# Revit family: Projector_Mount_Accessory-Chief-Extension-Fixed-CMS006
name_source: partatom
category: Specialty Equipment
revit_build: Autodesk Revit MEP 2012 (Build: 20110309_2315(x64)
units: mm (PartAtom-declared; Revit-internal decimal feet)

## types (3) — shared parameters
04 CSI = 11 52 00
95 CSI = 11130
Assembly Code = E1020500
CAD Drawings URL = http://downloads.chiefmfg.com
Certification = TÜV Certified, UL Listed
Cost Info = http://www.chiefmfg.com
Description = Projector Mount Accessory - Extension Column, Fixed
Height = 0' - 1 29/32"
Manual and Installation URL = http://downloads.chiefmfg.com
Manufacturer = Chief
Manufacturer Fax = 877.894.6918
Product Line = Extension-Fixed
Product Page URL = http://www.chiefmfg.com
Subcategory = Projector Mount Accessories
URL = http://www.chiefmfg.com
Weight Capacity = 500.00 lb
Width = 0' - 1 29/32"
ecoScorecard Product Page = http://ecoscorecard.com

## per-type parameters (varying)
| type | Material Finish | Product Color |
| CMS006 | Metal - Chief - Black | Black |
| CMS006S | Metal - Chief - Silver | Silver |
| CMS006W | Metal - Chief - White | White |

note: column(s) folded — value = type name in every type: Model

## geometry (parser evidence)
native form markers: Blend x2, Sweep x1
no freeform markers — native parametric forms only
